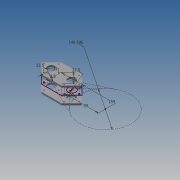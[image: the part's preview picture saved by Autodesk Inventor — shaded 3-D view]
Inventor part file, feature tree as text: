
AUTODESK INVENTOR PART (.ipt)
format: ipt  version: 2013 (Build 170138000, 138)  size: 126,976 bytes
history: native  units: mm
features: extrude x2, sketch x1
ambient origin geometry x8: Origin, YZ Plane, XZ Plane, XY Plane, X Axis, Y Axis, Z Axis, Center Point
bodies: Solid1 (feature_tree)
feature tree (3):
  sketch  "Sketch1"  dims[d0=10.185916mm d2=149.605647mm d3=99.0mm d4=50.0mm d5=0.0mm d6=159.0mm d7=42.0mm d8=22.5mm d9=22.5mm d10=31.0mm d11=3.5mm d15=40.0mm d16=0.0mm d17=3.0mm]
  extrude  "Extrusion1"  Depth=149.605647mm
  extrude  "Extrusion3"  Depth=99.0mm
